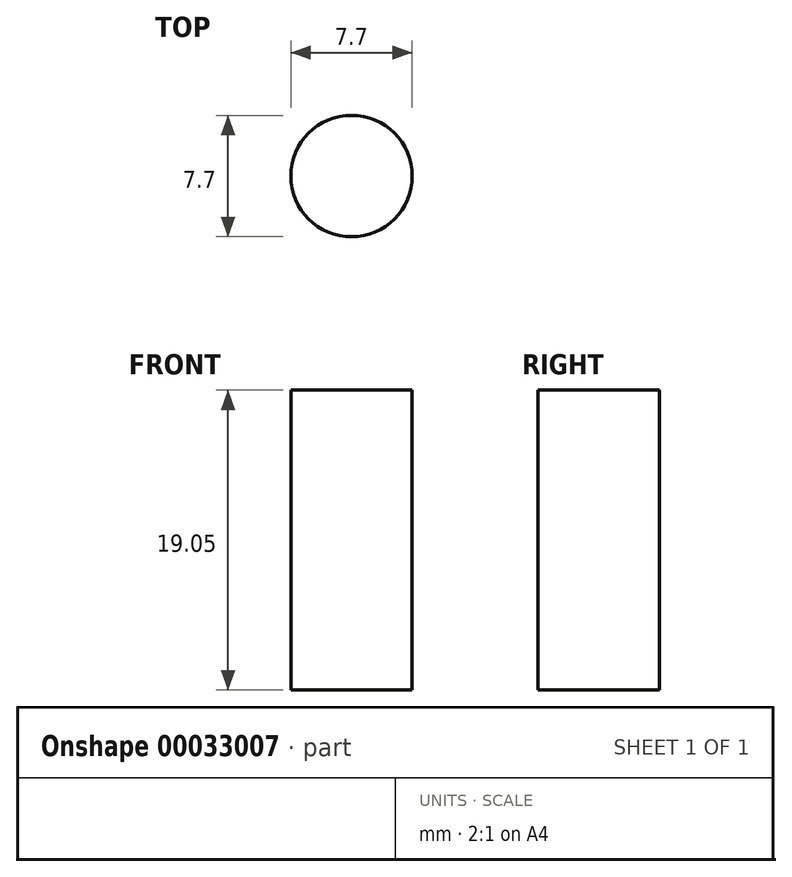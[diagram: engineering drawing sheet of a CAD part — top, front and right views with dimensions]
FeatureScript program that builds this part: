
annotation { "Feature Type Name" : "Feature", "Feature Type Description" : "" }
export const myFeature = defineFeature(function(context is Context, id is Id, definition is map)
    precondition{}
    {
        {
            var Q0;
            Q0=qCreatedBy(makeId("Top.planeOp"),FACE);
            var sketch = newSketch(context, id + "F0", { "sketchPlane" : qUnion([Q0])});
            skCircle(sketch, "E0", {"center": v(0, 0) * mm, "radius": 3.85 * mm});
            skSolve(sketch);
        }
        {
            var Q0;
            Q0=makeQuery(id+"F0.imprint","IMPRINT",FACE,{"disambiguationData":[TD([[makeQuery(id+"F0.imprint","IMPRINT",EDGE,{"derivedFrom":sQuery(id+"F0.wireOp",EDGE,"E0")}),1.0]])]});
            extrude(context, id + "F1", {"entities" : qUnion([Q0]), "depth" : 19.05 * mm});
        }
    });
